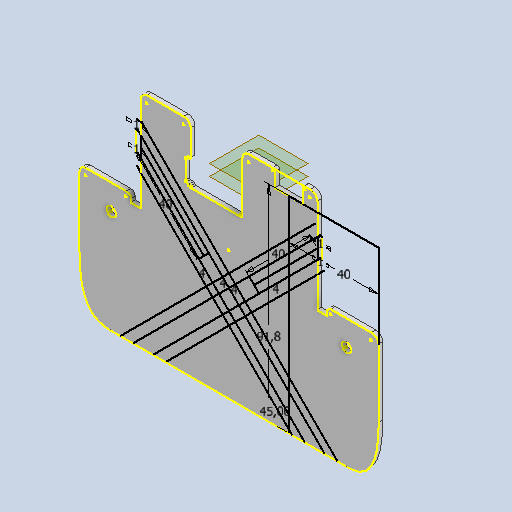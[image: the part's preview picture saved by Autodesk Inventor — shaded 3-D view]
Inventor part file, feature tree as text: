
AUTODESK INVENTOR PART (.ipt)
format: ipt  version: 2022 (Build 260153000, 153)  size: 517,120 bytes
history: native  units: mm
features: reference x19, other x17, sketch x10, extrude x8, projected_geometry x6, fillet x4, mirror x1
ambient origin geometry x8: Origin, YZ Plane, XZ Plane, XY Plane, X Axis, Y Axis, Z Axis, Center Point
bodies: Body1 (feature_tree)
feature tree (65):
  other  "Твердое тело1"
  extrude  "Выдавливание1"  Depth=81.0mm
  other  "РабПлоскость2"
  extrude  "Выдавливание2"  Depth=105.0mm
  other  "РабПлоскость3"
  extrude  "Выдавливание3"  Depth=2.0mm TaperAngle=0.0deg
  extrude  "Выдавливание4"  Depth=2.0mm
  extrude  "Выдавливание7"  Depth=2.0mm
  fillet  "Сопряжение1"  Radius=10.0mm
  fillet  "Сопряжение2"  Radius=2.0mm
  extrude  "Выдавливание8"  Depth=2.0mm
  fillet  "Сопряжение3"  Radius=11.0mm
  mirror  "Зеркальное отражение1"
  extrude  "Выдавливание10"  Depth=28.838075mm
  sketch  "Эскиз12"
  sketch  "Эскиз13"
  extrude  "Выдавливание11"  Depth=3.0mm
  fillet  "Сопряжение5"  Radius=1.0mm
  sketch  "Эскиз15"
  reference  "Ссылка1"
  reference  "Ссылка2"
  reference  "Ссылка3"
  reference  "Ссылка4"
  sketch  "Эскиз3"
  sketch  "Эскиз4"
  projected_geometry  "Спроецированная петля1"
  reference  "Ссылка16"
  sketch  "Эскиз5"
  reference  "Ссылка17"
  reference  "Ссылка18"
  reference  "Ссылка19"
  reference  "Ссылка20"
  sketch  "Эскиз8"
  reference  "Ссылка28"
  sketch  "Эскиз9"
  projected_geometry  "Спроецированная петля3"
  reference  "Ссылка29"
  reference  "Ссылка31"
  projected_geometry  "Спроецированная петля4"
  reference  "Ссылка32"
  sketch  "Эскиз11"
  reference  "Ссылка33"
  reference  "Ссылка34"
  projected_geometry  "Спроецированная петля5"
  reference  "Ссылка35"
  reference  "Ссылка36"
  reference  "Ссылка37"
  projected_geometry  "Спроецированная петля6"
  sketch  "Эскиз14"
  reference  "Ссылка38"
  projected_geometry  "Спроецированная петля7"
  other  "<userpath>\Documents\Git\MZCAT_2024\MZCAT_2.iam"
  other  "MZCAT_2.iam"
  other  "FastBattery:1"
  other  "metal_cap:1"
  other  "<userpath>\Documents\Git\MZCAT_2024_construction\MZCAT_2024_RPI_2\MZCAT_4.iam"
  other  "MZCAT_4.iam"
  other  "CAT_protector:1"
  other  "base plate:2"
  other  "base plate:1"
  other  "<userpath>\Documents\Git\MZCAT_2024\MZCAT_3.iam"
  other  "MZCAT_3.iam"
  other  "akkum_cup:1"
  other  "motherboard_plate:1"
  other  "lidar_krestovina_base:1"
